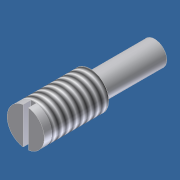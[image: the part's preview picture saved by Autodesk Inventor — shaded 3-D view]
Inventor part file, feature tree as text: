
AUTODESK INVENTOR PART (.ipt)
format: ipt  version: unknown  size: 183,296 bytes
history: native  units: in
note: dims shown in document units (in); Inventor stores cm internally (conversion verified against a paired STEP export)
features: sketch x2, revolve x1, thread x1, plane x1, extrude x1
ambient origin geometry x8: Origin, YZ Plane, XZ Plane, XY Plane, X Axis, Y Axis, Z Axis, Center Point
bodies: Solid1 (feature_tree)
feature tree (6):
  revolve  "Revolution1"  [1 undecoded]
  thread  "Thread3"  [1 undecoded]
  plane  "Work Plane2"
  extrude  "Extrusion2"  Depth=0.375in
  sketch  "Sketch1"  dims[d0=0.75in d1=0.0705in d4=0.108in]
  sketch  "Sketch3"  dims[d5=90.0deg d15=0.375in d16=0.375in d17=0.046in d18=0.0155in d19=0.0155in d20=0.046in d21=1.0in d22=0.0in]
note: 2 required parameter values undecoded (feature->parameter linkage not recoverable at this tier; creation-order binding heuristic only, values carry confidence <= 0.55)